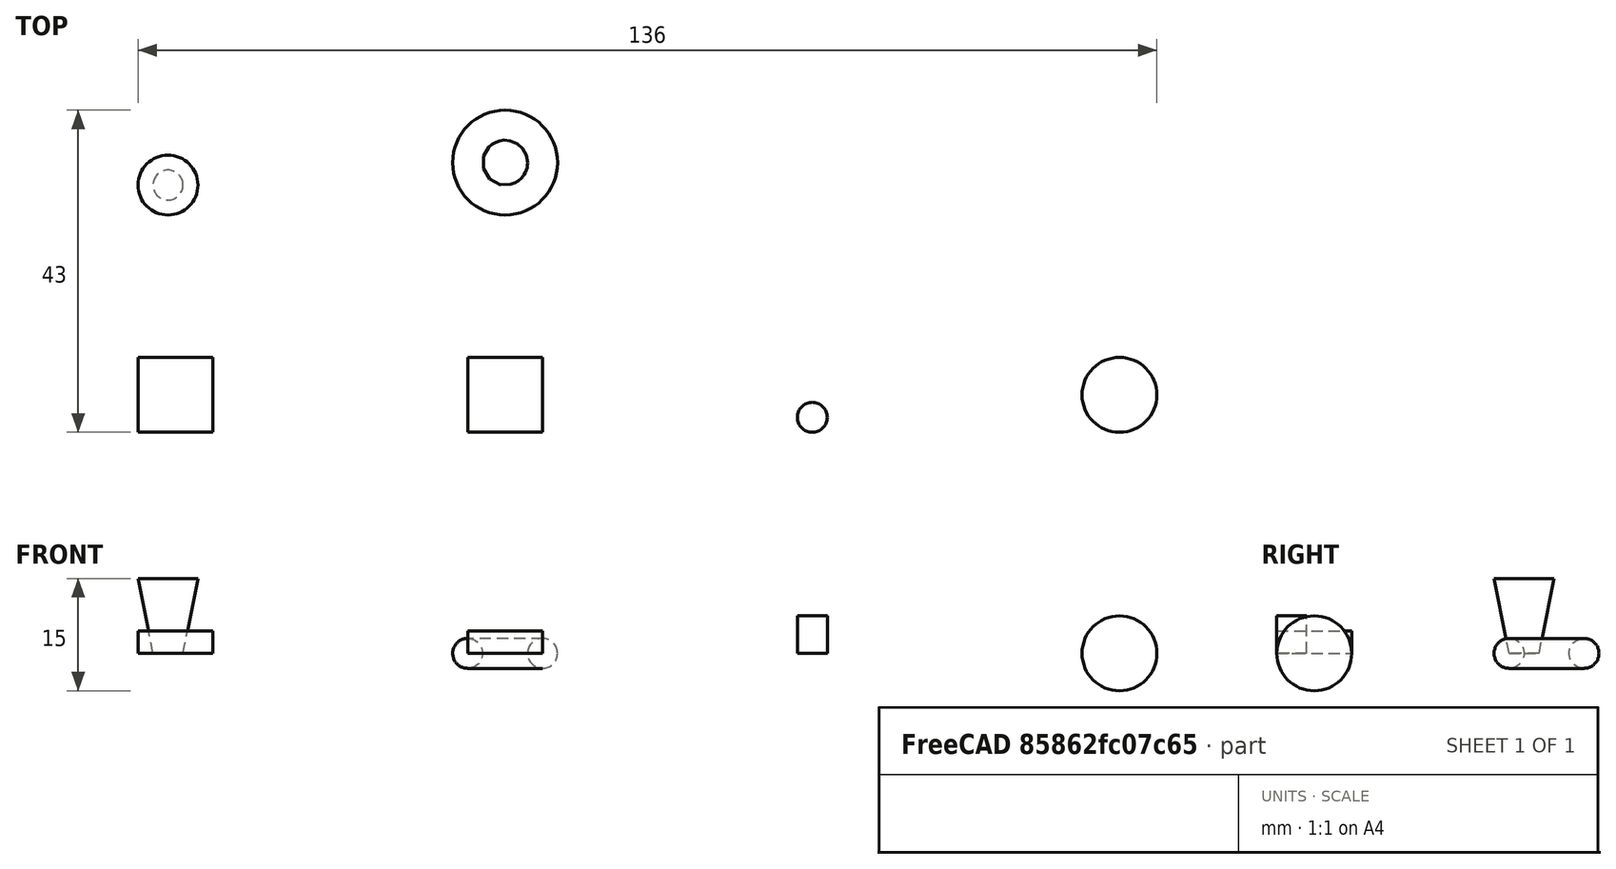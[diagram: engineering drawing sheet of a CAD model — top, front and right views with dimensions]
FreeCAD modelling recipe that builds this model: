
FCSTD DOCUMENT  (FreeCAD 0.16R6703 (Git))
Label: shapes-test-result
License: All rights reserved
LicenseURL: http://en.wikipedia.org/wiki/All_rights_reserved
objects: Part::Box×2, Part::Cylinder×1, Part::Sphere×1, Part::Cone×1, Part::Torus×1
note: 6 computed .brp shape members not serialized (recipe doc carries the construction recipe); baked Part::Feature solids carry a one-line shape summary decoded from their .brp

FEATURE [Part::Box] Box  label="Cube"
  Height = 3
  Length = 10
  Width = 10
FEATURE [Part::Box] Box001  label="Cube001"
  Height = 3
  Length = 10
  Placement = pos=(44,0,0) rot=(0,0,1;0rad)
  Width = 10
FEATURE [Part::Cylinder] Cylinder
  Angle = 360
  Height = 5
  Placement = pos=(90,2,0) rot=(0,0,1;0rad)
  Radius = 2
FEATURE [Part::Sphere] Sphere
  Angle1 = -90
  Angle2 = 90
  Angle3 = 360
  Placement = pos=(131,4.9978,0) rot=(0,0,1;0rad)
  Radius = 5
FEATURE [Part::Cone] Cone
  Angle = 360
  Height = 10
  Placement = pos=(4,33,0) rot=(0,0,1;0rad)
  Radius1 = 2
  Radius2 = 4
FEATURE [Part::Torus] Torus
  Angle1 = -180
  Angle2 = 180
  Angle3 = 360
  Placement = pos=(49,36,0) rot=(0,0,1;0rad)
  Radius1 = 5
  Radius2 = 2
